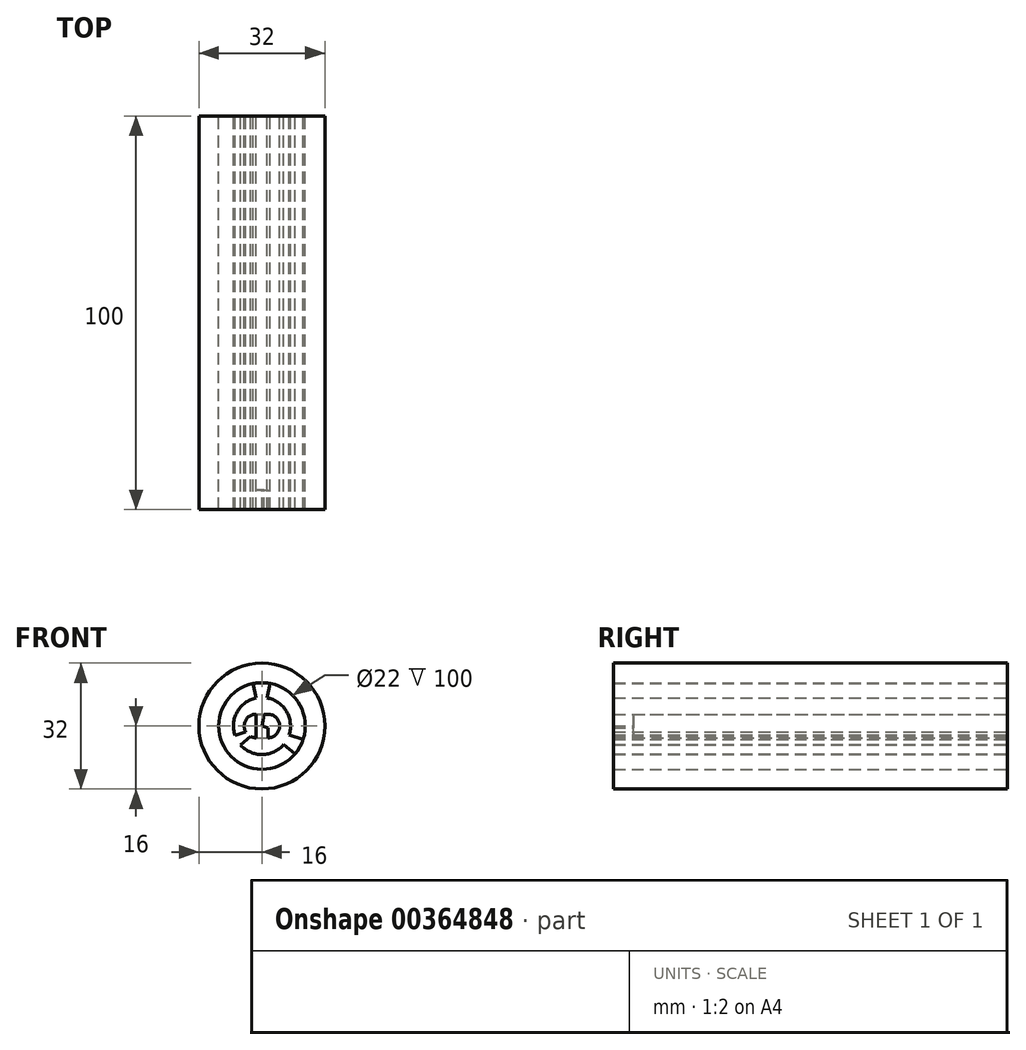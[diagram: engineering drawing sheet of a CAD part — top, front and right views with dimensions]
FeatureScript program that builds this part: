
annotation { "Feature Type Name" : "Feature", "Feature Type Description" : "" }
export const myFeature = defineFeature(function(context is Context, id is Id, definition is map)
    precondition{}
    {
        {
            var Q0;
            Q0=qCreatedBy(makeId("Front.planeOp"),FACE);
            var sketch = newSketch(context, id + "F0", { "sketchPlane" : qUnion([Q0])});
            skCircle(sketch, "E0", {"center": v(0, 0) * mm, "radius": 11 * mm});
            skCircle(sketch, "E1", {"center": v(0, 0) * mm, "radius": 16 * mm});
            skSolve(sketch);
        }
        {
            var Q0;
            Q0=makeQuery(id+"F0.imprint","IMPRINT",FACE,{"disambiguationData":[TD([[makeQuery(id+"F0.imprint","IMPRINT",EDGE,{"derivedFrom":sQuery(id+"F0.wireOp",EDGE,"E0")}),-1.0]])]});
            extrude(context, id + "F1", {"entities" : qUnion([Q0]), "depth" : 100 * mm});
        }
        {
            var Q0;
            Q0=makeQuery(id+"F1.opExtrude","CAP_FACE",FACE,{"disambiguationData":[OSD([sQuery(id+"F0.wireOp",EDGE,"E0"),sQuery(id+"F0.wireOp",EDGE,"E1")])],"isStart":true});
            var sketch = newSketch(context, id + "F2", { "sketchPlane" : qUnion([Q0])});
            skLineSegment(sketch, "E2", {"start": v(0, 0) * mm, "end": v(-10.46, -3.4) * mm});
            skLineSegment(sketch, "E3", {"start": v(0, 0) * mm, "end": v(2.29, 10.76) * mm});
            skLineSegment(sketch, "E4", {"start": v(0, 0) * mm, "end": v(8.17, -7.36) * mm});
            skCircle(sketch, "E5", {"center": v(0, 0) * mm, "radius": 7.25 * mm});
            skLineSegment(sketch, "E6", {"start": v(0, 0) * mm, "end": v(0, 3) * mm});
            skLineSegment(sketch, "E7", {"start": v(0, 3) * mm, "end": v(-1.5, 3) * mm});
            skLineSegment(sketch, "E8", {"start": v(-1.5, 3) * mm, "end": v(1.5, 3) * mm});
            skPoint(sketch, "E8.endSnap0", {"position": v(-0.75, 3) * mm});
            skLineSegment(sketch, "E9", {"start": v(1.5, 3) * mm, "end": v(1.5, -3) * mm});
            skLineSegment(sketch, "E10", {"start": v(1.5, -3) * mm, "end": v(-1.5, -3) * mm});
            skLineSegment(sketch, "E11", {"start": v(-1.5, -3) * mm, "end": v(-1.5, 3) * mm});
            skArc(sketch, "E12", {"start": v(-1.5, 3) * mm, "mid": v(-4.5, 0) * mm, "end": v(-1.5, -3) * mm});
            skArc(sketch, "E13", {"start": v(1.5, -3) * mm, "mid": v(4.5, 0) * mm, "end": v(1.5, 3) * mm});
            skLineSegment(sketch, "E14", {"start": v(-8.36, -7.14) * mm, "end": v(0, 0) * mm});
            skLineSegment(sketch, "E15", {"start": v(0, 0) * mm, "end": v(10.37, -3.67) * mm});
            skLineSegment(sketch, "E16", {"start": v(0, 0) * mm, "end": v(3.67, 10.37) * mm, "construction": true});
            skLineSegment(sketch, "E17", {"start": v(0, 0) * mm, "end": v(-2, 10.82) * mm});
            skSolve(sketch);
        }
        {
            var Q0;
            {var subQ0=sQuery(id+"F2.wireOp",EDGE,"E2");var subQ1=makeQuery(id+"F1.opExtrude","CAP_EDGE",EDGE,{"disambiguationData":[OSD([sQuery(id+"F0.wireOp",EDGE,"E0")])],"isStart":true});var subQ2=makeQuery(id+"F2.imprint","INTERSECT",VERTEX,{"derivedFrom":[subQ1,subQ0]});Q0=makeQuery(id+"F2.imprint","IMPRINT",FACE,{"disambiguationData":[TD([[makeQuery(id+"F2.imprint","IMPRINT",EDGE,{"disambiguationData":[TD([[subQ2,1.0]])],"derivedFrom":subQ0}),1.0]])]});}
            var Q1;
            {var subQ0=sQuery(id+"F2.wireOp",EDGE,"E3");var subQ1=makeQuery(id+"F1.opExtrude","CAP_EDGE",EDGE,{"disambiguationData":[OSD([sQuery(id+"F0.wireOp",EDGE,"E0")])],"isStart":true});var subQ2=makeQuery(id+"F2.imprint","INTERSECT",VERTEX,{"derivedFrom":[subQ1,subQ0]});Q1=makeQuery(id+"F2.imprint","IMPRINT",FACE,{"disambiguationData":[TD([[makeQuery(id+"F2.imprint","IMPRINT",EDGE,{"disambiguationData":[TD([[subQ2,1.0]])],"derivedFrom":subQ0}),1.0]])]});}
            var Q2;
            {var subQ0=sQuery(id+"F2.wireOp",EDGE,"E4");var subQ1=makeQuery(id+"F1.opExtrude","CAP_EDGE",EDGE,{"disambiguationData":[OSD([sQuery(id+"F0.wireOp",EDGE,"E0")])],"isStart":true});var subQ2=makeQuery(id+"F2.imprint","INTERSECT",VERTEX,{"derivedFrom":[subQ1,subQ0]});Q2=makeQuery(id+"F2.imprint","IMPRINT",FACE,{"disambiguationData":[TD([[makeQuery(id+"F2.imprint","IMPRINT",EDGE,{"disambiguationData":[TD([[subQ2,1.0]])],"derivedFrom":subQ0}),1.0]])]});}
            var Q3;
            {var subQ0=sQuery(id+"F2.wireOp",EDGE,"E13");var subQ3=sQuery(id+"F2.wireOp",EDGE,"E3");var subQ4=makeQuery(id+"F2.imprint","INTERSECT",VERTEX,{"derivedFrom":[subQ3,subQ0]});Q3=makeQuery(id+"F2.imprint","IMPRINT",FACE,{"disambiguationData":[TD([[makeQuery(id+"F2.imprint","IMPRINT",EDGE,{"disambiguationData":[TD([[subQ4,-1.0]])],"derivedFrom":subQ3}),1.0]])]});}
            var Q4;
            {var subQ4=sQuery(id+"F2.wireOp",EDGE,"E12");var subQ6=sQuery(id+"F2.wireOp",EDGE,"E2");var subQ7=makeQuery(id+"F2.imprint","INTERSECT",VERTEX,{"derivedFrom":[subQ6,subQ4]});Q4=makeQuery(id+"F2.imprint","IMPRINT",FACE,{"disambiguationData":[TD([[makeQuery(id+"F2.imprint","IMPRINT",EDGE,{"disambiguationData":[TD([[subQ7,-1.0]])],"derivedFrom":subQ6}),-1.0]])]});}
            var Q5;
            {var subQ0=sQuery(id+"F2.wireOp",EDGE,"E12");var subQ1=sQuery(id+"F2.wireOp",EDGE,"E2");var subQ2=makeQuery(id+"F2.imprint","INTERSECT",VERTEX,{"derivedFrom":[subQ1,subQ0]});Q5=makeQuery(id+"F2.imprint","IMPRINT",FACE,{"disambiguationData":[TD([[makeQuery(id+"F2.imprint","IMPRINT",EDGE,{"disambiguationData":[TD([[subQ2,-1.0]])],"derivedFrom":subQ1}),1.0]])]});}
            var Q6;
            {var subQ1=sQuery(id+"F2.wireOp",EDGE,"E4");var subQ3=sQuery(id+"F2.wireOp",EDGE,"E10");var subQ4=makeQuery(id+"F2.imprint","INTERSECT",VERTEX,{"derivedFrom":[subQ1,subQ3]});Q6=makeQuery(id+"F2.imprint","IMPRINT",FACE,{"disambiguationData":[TD([[makeQuery(id+"F2.imprint","IMPRINT",EDGE,{"disambiguationData":[TD([[subQ4,-1.0]])],"derivedFrom":subQ3}),-1.0]])]});}
            var Q7;
            {var subQ0=sQuery(id+"F2.wireOp",EDGE,"E15");var subQ5=sQuery(id+"F2.wireOp",EDGE,"E9");var subQ7=makeQuery(id+"F2.imprint","INTERSECT",VERTEX,{"derivedFrom":[subQ5,subQ0]});Q7=makeQuery(id+"F2.imprint","IMPRINT",FACE,{"disambiguationData":[TD([[makeQuery(id+"F2.imprint","IMPRINT",EDGE,{"disambiguationData":[TD([[subQ7,-1.0]])],"derivedFrom":subQ5}),-1.0]])]});}
            var Q8;
            {var subQ1=sQuery(id+"F2.wireOp",EDGE,"E3");var subQ3=sQuery(id+"F2.wireOp",EDGE,"E9");var subQ4=makeQuery(id+"F2.imprint","INTERSECT",VERTEX,{"derivedFrom":[subQ1,subQ3]});Q8=makeQuery(id+"F2.imprint","IMPRINT",FACE,{"disambiguationData":[TD([[makeQuery(id+"F2.imprint","IMPRINT",EDGE,{"disambiguationData":[TD([[subQ4,-1.0]])],"derivedFrom":subQ3}),-1.0]])]});}
            var Q9;
            {var subQ0=sQuery(id+"F2.wireOp",EDGE,"E6");Q9=makeQuery(id+"F2.imprint","IMPRINT",FACE,{"disambiguationData":[TD([[makeQuery(id+"F2.imprint","IMPRINT",EDGE,{"derivedFrom":subQ0}),1.0]])]});}
            var Q10;
            {var subQ1=sQuery(id+"F2.wireOp",EDGE,"E2");var subQ3=sQuery(id+"F2.wireOp",EDGE,"E11");var subQ4=makeQuery(id+"F2.imprint","INTERSECT",VERTEX,{"derivedFrom":[subQ1,subQ3]});Q10=makeQuery(id+"F2.imprint","IMPRINT",FACE,{"disambiguationData":[TD([[makeQuery(id+"F2.imprint","IMPRINT",EDGE,{"disambiguationData":[TD([[subQ4,1.0]])],"derivedFrom":subQ3}),-1.0]])]});}
            var Q11;
            {var subQ0=sQuery(id+"F2.wireOp",EDGE,"E6");Q11=makeQuery(id+"F2.imprint","IMPRINT",FACE,{"disambiguationData":[TD([[makeQuery(id+"F2.imprint","IMPRINT",EDGE,{"derivedFrom":subQ0}),-1.0]])]});}
            var Q12;
            {var subQ0=sQuery(id+"F2.wireOp",EDGE,"E17");var subQ5=sQuery(id+"F2.wireOp",EDGE,"E8");var subQ7=makeQuery(id+"F2.imprint","INTERSECT",VERTEX,{"derivedFrom":[subQ5,subQ0]});Q12=makeQuery(id+"F2.imprint","IMPRINT",FACE,{"disambiguationData":[TD([[makeQuery(id+"F2.imprint","IMPRINT",EDGE,{"disambiguationData":[TD([[subQ7,-1.0]])],"derivedFrom":subQ5}),-1.0]])]});}
            var Q13;
            {var subQ1=sQuery(id+"F2.wireOp",EDGE,"E8");var subQ5=sQuery(id+"F2.wireOp",EDGE,"E3");var subQ6=makeQuery(id+"F2.imprint","INTERSECT",VERTEX,{"derivedFrom":[subQ5,subQ1]});Q13=makeQuery(id+"F2.imprint","IMPRINT",FACE,{"disambiguationData":[TD([[makeQuery(id+"F2.imprint","IMPRINT",EDGE,{"disambiguationData":[TD([[subQ6,-1.0]])],"derivedFrom":subQ5}),-1.0]])]});}
            var Q14;
            {var subQ1=sQuery(id+"F2.wireOp",EDGE,"E10");Q14=makeQuery(id+"F2.imprint","IMPRINT",FACE,{"disambiguationData":[TD([[makeQuery(id+"F2.imprint","IMPRINT",EDGE,{"derivedFrom":subQ1}),1.0]])]});}
            var Q15;
            {var subQ0=sQuery(id+"F2.wireOp",EDGE,"E8");var subQ5=sQuery(id+"F2.wireOp",EDGE,"E3");var subQ8=makeQuery(id+"F2.imprint","INTERSECT",VERTEX,{"derivedFrom":[subQ5,subQ0]});Q15=makeQuery(id+"F2.imprint","IMPRINT",FACE,{"disambiguationData":[TD([[makeQuery(id+"F2.imprint","IMPRINT",EDGE,{"disambiguationData":[TD([[subQ8,-1.0]])],"derivedFrom":subQ5}),1.0]])]});}
            var Q16;
            {var subQ0=sQuery(id+"F2.wireOp",EDGE,"E17");var subQ5=sQuery(id+"F2.wireOp",EDGE,"E8");var subQ7=makeQuery(id+"F2.imprint","INTERSECT",VERTEX,{"derivedFrom":[subQ5,subQ0]});Q16=makeQuery(id+"F2.imprint","IMPRINT",FACE,{"disambiguationData":[TD([[makeQuery(id+"F2.imprint","IMPRINT",EDGE,{"disambiguationData":[TD([[subQ7,1.0]])],"derivedFrom":subQ5}),-1.0]])]});}
            var Q17;
            {var subQ1=sQuery(id+"F2.wireOp",EDGE,"E3");var subQ3=sQuery(id+"F2.wireOp",EDGE,"E8");var subQ4=makeQuery(id+"F2.imprint","INTERSECT",VERTEX,{"derivedFrom":[subQ1,subQ3]});Q17=makeQuery(id+"F2.imprint","IMPRINT",FACE,{"disambiguationData":[TD([[makeQuery(id+"F2.imprint","IMPRINT",EDGE,{"disambiguationData":[TD([[subQ4,-1.0]])],"derivedFrom":subQ3}),-1.0]])]});}
            var Q18;
            {var subQ0=sQuery(id+"F2.wireOp",EDGE,"E13");var subQ1=sQuery(id+"F2.wireOp",EDGE,"E4");var subQ2=makeQuery(id+"F2.imprint","INTERSECT",VERTEX,{"derivedFrom":[subQ1,subQ0]});Q18=makeQuery(id+"F2.imprint","IMPRINT",FACE,{"disambiguationData":[TD([[makeQuery(id+"F2.imprint","IMPRINT",EDGE,{"disambiguationData":[TD([[subQ2,-1.0]])],"derivedFrom":subQ1}),1.0]])]});}
            var Q19;
            {var subQ0=sQuery(id+"F2.wireOp",EDGE,"E4");var subQ1=makeQuery(id+"F1.opExtrude","CAP_EDGE",EDGE,{"disambiguationData":[OSD([sQuery(id+"F0.wireOp",EDGE,"E0")])],"isStart":true});var subQ2=makeQuery(id+"F2.imprint","INTERSECT",VERTEX,{"derivedFrom":[subQ1,subQ0]});Q19=makeQuery(id+"F2.imprint","IMPRINT",FACE,{"disambiguationData":[TD([[makeQuery(id+"F2.imprint","IMPRINT",EDGE,{"disambiguationData":[TD([[subQ2,1.0]])],"derivedFrom":subQ0}),1.0]])]});}
            extrude(context, id + "F3", {"entities" : qUnion([Q0, Q1, Q2, Q3, Q4, Q5, Q6, Q7, Q8, Q9, Q10, Q11, Q12, Q13, Q14, Q15, Q16, Q17, Q18, Q19]), "oppositeDirection" : true, "depth" : 100 * mm});
        }
        {
            var Q0;
            {var subQ1=sQuery(id+"F2.wireOp",EDGE,"E4");var subQ3=sQuery(id+"F2.wireOp",EDGE,"E10");var subQ4=makeQuery(id+"F2.imprint","INTERSECT",VERTEX,{"derivedFrom":[subQ1,subQ3]});Q0=makeQuery(id+"F2.imprint","IMPRINT",FACE,{"disambiguationData":[TD([[makeQuery(id+"F2.imprint","IMPRINT",EDGE,{"disambiguationData":[TD([[subQ4,-1.0]])],"derivedFrom":subQ3}),-1.0]])]});}
            var Q1;
            {var subQ0=sQuery(id+"F2.wireOp",EDGE,"E15");var subQ5=sQuery(id+"F2.wireOp",EDGE,"E9");var subQ7=makeQuery(id+"F2.imprint","INTERSECT",VERTEX,{"derivedFrom":[subQ5,subQ0]});Q1=makeQuery(id+"F2.imprint","IMPRINT",FACE,{"disambiguationData":[TD([[makeQuery(id+"F2.imprint","IMPRINT",EDGE,{"disambiguationData":[TD([[subQ7,-1.0]])],"derivedFrom":subQ5}),-1.0]])]});}
            var Q2;
            {var subQ1=sQuery(id+"F2.wireOp",EDGE,"E3");var subQ3=sQuery(id+"F2.wireOp",EDGE,"E9");var subQ4=makeQuery(id+"F2.imprint","INTERSECT",VERTEX,{"derivedFrom":[subQ1,subQ3]});Q2=makeQuery(id+"F2.imprint","IMPRINT",FACE,{"disambiguationData":[TD([[makeQuery(id+"F2.imprint","IMPRINT",EDGE,{"disambiguationData":[TD([[subQ4,-1.0]])],"derivedFrom":subQ3}),-1.0]])]});}
            var Q3;
            {var subQ0=sQuery(id+"F2.wireOp",EDGE,"E17");var subQ5=sQuery(id+"F2.wireOp",EDGE,"E8");var subQ7=makeQuery(id+"F2.imprint","INTERSECT",VERTEX,{"derivedFrom":[subQ5,subQ0]});Q3=makeQuery(id+"F2.imprint","IMPRINT",FACE,{"disambiguationData":[TD([[makeQuery(id+"F2.imprint","IMPRINT",EDGE,{"disambiguationData":[TD([[subQ7,-1.0]])],"derivedFrom":subQ5}),-1.0]])]});}
            var Q4;
            {var subQ0=sQuery(id+"F2.wireOp",EDGE,"E6");Q4=makeQuery(id+"F2.imprint","IMPRINT",FACE,{"disambiguationData":[TD([[makeQuery(id+"F2.imprint","IMPRINT",EDGE,{"derivedFrom":subQ0}),-1.0]])]});}
            var Q5;
            {var subQ0=sQuery(id+"F2.wireOp",EDGE,"E6");Q5=makeQuery(id+"F2.imprint","IMPRINT",FACE,{"disambiguationData":[TD([[makeQuery(id+"F2.imprint","IMPRINT",EDGE,{"derivedFrom":subQ0}),1.0]])]});}
            var Q6;
            {var subQ1=sQuery(id+"F2.wireOp",EDGE,"E2");var subQ3=sQuery(id+"F2.wireOp",EDGE,"E11");var subQ4=makeQuery(id+"F2.imprint","INTERSECT",VERTEX,{"derivedFrom":[subQ1,subQ3]});Q6=makeQuery(id+"F2.imprint","IMPRINT",FACE,{"disambiguationData":[TD([[makeQuery(id+"F2.imprint","IMPRINT",EDGE,{"disambiguationData":[TD([[subQ4,1.0]])],"derivedFrom":subQ3}),-1.0]])]});}
            var Q7;
            {var subQ1=sQuery(id+"F2.wireOp",EDGE,"E3");var subQ3=sQuery(id+"F2.wireOp",EDGE,"E8");var subQ4=makeQuery(id+"F2.imprint","INTERSECT",VERTEX,{"derivedFrom":[subQ1,subQ3]});Q7=makeQuery(id+"F2.imprint","IMPRINT",FACE,{"disambiguationData":[TD([[makeQuery(id+"F2.imprint","IMPRINT",EDGE,{"disambiguationData":[TD([[subQ4,-1.0]])],"derivedFrom":subQ3}),-1.0]])]});}
            var Q8;
            {var subQ0=sQuery(id+"F2.wireOp",EDGE,"E17");var subQ5=sQuery(id+"F2.wireOp",EDGE,"E8");var subQ7=makeQuery(id+"F2.imprint","INTERSECT",VERTEX,{"derivedFrom":[subQ5,subQ0]});Q8=makeQuery(id+"F2.imprint","IMPRINT",FACE,{"disambiguationData":[TD([[makeQuery(id+"F2.imprint","IMPRINT",EDGE,{"disambiguationData":[TD([[subQ7,1.0]])],"derivedFrom":subQ5}),-1.0]])]});}
            extrude(context, id + "F4", {"entities" : qUnion([Q0, Q1, Q2, Q3, Q4, Q5, Q6, Q7, Q8]), "operationType" : NewBodyOperationType.REMOVE, "oppositeDirection" : true, "depth" : 95 * mm});
        }
    });
